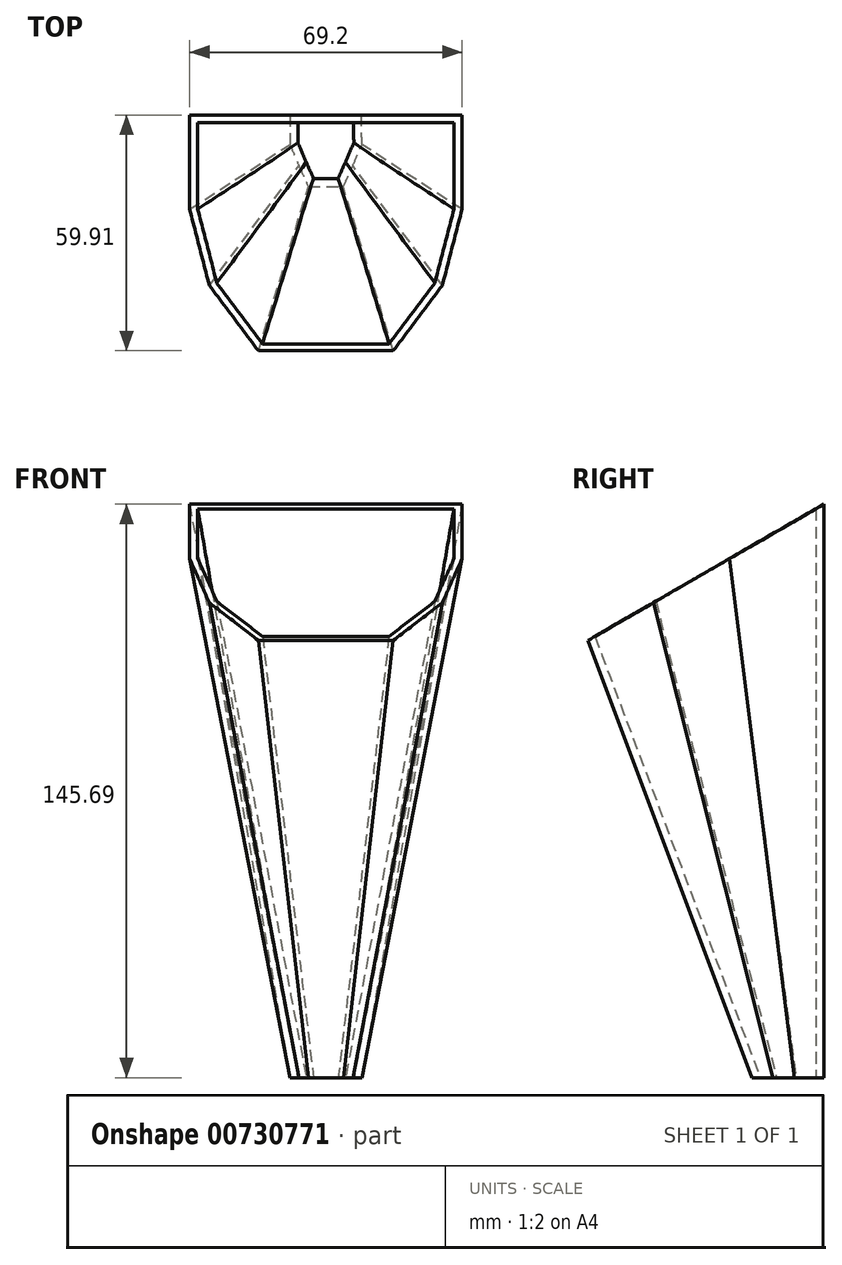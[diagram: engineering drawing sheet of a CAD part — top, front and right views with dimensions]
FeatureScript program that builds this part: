
annotation { "Feature Type Name" : "Feature", "Feature Type Description" : "" }
export const myFeature = defineFeature(function(context is Context, id is Id, definition is map)
    precondition{}
    {
        {
            var Q0;
            Q0=qCreatedBy(makeId("Top.planeOp"),FACE);
            var sketch = newSketch(context, id + "F0", { "sketchPlane" : qUnion([Q0])});
            skLineSegment(sketch, "E0", {"start": v(-50.65, 0) * mm, "end": v(54.5, 0) * mm, "construction": true});
            skSolve(sketch);
        }
        {
            var Q0;
            Q0=sQuery(id+"F0.wireOp",EDGE,"E0");
            cPlane(context, id + "F1", {"entities" : qUnion([Q0]), "cplaneType" : CPlaneType.LINE_ANGLE, "offset" : 25 * mm, "angle" : 300 * degree, "width" : 150 * mm, "height" : 150 * mm});
        }
        {
            var Q0;
            Q0=qCreatedBy(id+"F1.planeOp",FACE);
            var sketch = newSketch(context, id + "F2", { "sketchPlane" : qUnion([Q0])});
            skLineSegment(sketch, "E1", {"start": v(-35, 0) * mm, "end": v(35, 0) * mm});
            skLineSegment(sketch, "E2", {"start": v(35, 0) * mm, "end": v(35, 28) * mm});
            skLineSegment(sketch, "E3", {"start": v(17.35, 70) * mm, "end": v(0, 70) * mm});
            skCircle(sketch, "E4", {"center": v(0, 38) * mm, "radius": 25 * mm, "construction": true});
            skLineSegment(sketch, "E5", {"start": v(17.35, 70) * mm, "end": v(29.98, 50.6) * mm});
            skLineSegment(sketch, "E6", {"start": v(29.98, 50.6) * mm, "end": v(35, 28) * mm});
            skLineSegment(sketch, "E7", {"start": v(0, 0) * mm, "end": v(0, 70) * mm, "construction": true});
            skLineSegment(sketch, "E8.MirrorCS", {"start": v(-35, 0) * mm, "end": v(-35, 28) * mm});
            skLineSegment(sketch, "E9.MirrorCS", {"start": v(-29.98, 50.6) * mm, "end": v(-35, 28) * mm});
            skLineSegment(sketch, "E10.MirrorCS", {"start": v(-17.35, 70) * mm, "end": v(-29.98, 50.6) * mm});
            skLineSegment(sketch, "E11.MirrorCS", {"start": v(-17.35, 70) * mm, "end": v(0, 70) * mm});
            skSolve(sketch);
        }
        {
            var Q0;
            Q0=qCreatedBy(makeId("Top.planeOp"),FACE);
            cPlane(context, id + "F3", {"entities" : qUnion([Q0]), "cplaneType" : CPlaneType.OFFSET, "offset" : 150 * mm, "oppositeDirection" : true, "width" : 150 * mm, "height" : 150 * mm});
        }
        {
            var Q0;
            Q0=qCreatedBy(id+"F3.planeOp",FACE);
            var sketch = newSketch(context, id + "F4", { "sketchPlane" : qUnion([Q0])});
            skLineSegment(sketch, "E12", {"start": v(-8.75, 0) * mm, "end": v(-8.75, -7.25) * mm});
            skLineSegment(sketch, "E13", {"start": v(-4.2, -17.5) * mm, "end": v(0, -17.5) * mm});
            skCircle(sketch, "E14", {"center": v(0, -7.25) * mm, "radius": 6.25 * mm, "construction": true});
            skLineSegment(sketch, "E15", {"start": v(-8.75, 0) * mm, "end": v(0, 0) * mm});
            skLineSegment(sketch, "E16", {"start": v(0, 0) * mm, "end": v(0, -57.56) * mm, "construction": true});
            skLineSegment(sketch, "E17.MirrorCS", {"start": v(8.75, 0) * mm, "end": v(0, 0) * mm});
            skLineSegment(sketch, "E18", {"start": v(-8.75, -7.25) * mm, "end": v(-6.48, -12.38) * mm});
            skLineSegment(sketch, "E19", {"start": v(-6.48, -12.38) * mm, "end": v(-4.2, -17.5) * mm});
            skLineSegment(sketch, "E20.MirrorCS", {"start": v(4.2, -17.5) * mm, "end": v(0, -17.5) * mm});
            skLineSegment(sketch, "E21.MirrorCS", {"start": v(6.48, -12.38) * mm, "end": v(4.2, -17.5) * mm});
            skLineSegment(sketch, "E22.MirrorCS", {"start": v(8.75, -7.25) * mm, "end": v(6.48, -12.38) * mm});
            skLineSegment(sketch, "E23.MirrorCS", {"start": v(8.75, 0) * mm, "end": v(8.75, -7.25) * mm});
            skSolve(sketch);
        }
        {
            var Q0;
            Q0=makeQuery(id+"F2.imprint","IMPRINT",FACE,{"disambiguationData":[TD([[makeQuery(id+"F2.imprint","IMPRINT",EDGE,{"derivedFrom":sQuery(id+"F2.wireOp",EDGE,"E1")}),1.0]])]});
            var Q1;
            Q1=makeQuery(id+"F4.imprint","IMPRINT",FACE,{"disambiguationData":[TD([[makeQuery(id+"F4.imprint","IMPRINT",EDGE,{"derivedFrom":sQuery(id+"F4.wireOp",EDGE,"E12")}),1.0]])]});
            loft(context, id + "F5", {"sheetProfilesArray" : [{ "sheetProfileEntities" : qUnion([Q0]) }, { "sheetProfileEntities" : qUnion([Q1]) }]});
        }
        {
            var Q0;
            Q0=makeQuery(id+"F5.opLoft","SWEPT_FACE",FACE,{"disambiguationData":[OSD([sQuery(id+"F2.wireOp",EDGE,"E2"),sQuery(id+"F2.wireOp",EDGE,"E5"),sQuery(id+"F2.wireOp",EDGE,"E6"),sQuery(id+"F4.wireOp",EDGE,"E21.MirrorCS"),sQuery(id+"F4.wireOp",EDGE,"E22.MirrorCS"),sQuery(id+"F4.wireOp",EDGE,"E23.MirrorCS")])]});
            var Q1;
            Q1=makeQuery(id+"F5.opLoft","SWEPT_FACE",FACE,{"disambiguationData":[OSD([sQuery(id+"F2.wireOp",EDGE,"E1"),sQuery(id+"F2.wireOp",EDGE,"E2"),sQuery(id+"F2.wireOp",EDGE,"E6"),sQuery(id+"F4.wireOp",EDGE,"E17.MirrorCS"),sQuery(id+"F4.wireOp",EDGE,"E22.MirrorCS"),sQuery(id+"F4.wireOp",EDGE,"E23.MirrorCS")])]});
            var Q2;
            Q2=makeQuery(id+"F5.opLoft","SWEPT_FACE",FACE,{"disambiguationData":[OSD([sQuery(id+"F2.wireOp",EDGE,"E3"),sQuery(id+"F2.wireOp",EDGE,"E5"),sQuery(id+"F2.wireOp",EDGE,"E6"),sQuery(id+"F4.wireOp",EDGE,"E20.MirrorCS"),sQuery(id+"F4.wireOp",EDGE,"E21.MirrorCS"),sQuery(id+"F4.wireOp",EDGE,"E22.MirrorCS")])]});
            var Q3;
            Q3=makeQuery(id+"F5.opLoft","SWEPT_BODY",BODY,{"disambiguationData":[OSD([makeQuery(id+"F2.imprint","IMPRINT",FACE,{"disambiguationData":[TD([[makeQuery(id+"F2.imprint","IMPRINT",EDGE,{"derivedFrom":sQuery(id+"F2.wireOp",EDGE,"E1")}),1.0]])]}),makeQuery(id+"F4.imprint","IMPRINT",FACE,{"disambiguationData":[TD([[makeQuery(id+"F4.imprint","IMPRINT",EDGE,{"derivedFrom":sQuery(id+"F4.wireOp",EDGE,"E12")}),1.0]])]})])]});
            shell(context, id + "F6", {"isHollow" : true, "entities" : qUnion([Q0, Q1, Q2]), "parts" : qUnion([Q3]), "thickness" : 2 * mm});
        }
        {
            var Q0;
            Q0=makeQuery(id+"F5.opLoft","CAP_FACE",FACE,{"disambiguationData":[OSD([makeQuery(id+"F2.imprint","IMPRINT",FACE,{"disambiguationData":[TD([[makeQuery(id+"F2.imprint","IMPRINT",EDGE,{"derivedFrom":sQuery(id+"F2.wireOp",EDGE,"E1")}),1.0]])]})])],"isStart":true});
            var sketch = newSketch(context, id + "F7", { "sketchPlane" : qUnion([Q0])});
            skLineSegment(sketch, "E24.0", {"start": v(17.35, -70) * mm, "end": v(-17.35, -70) * mm});
            skLineSegment(sketch, "E24.1", {"start": v(29.98, -50.6) * mm, "end": v(17.35, -70) * mm});
            skLineSegment(sketch, "E24.2", {"start": v(35, -28) * mm, "end": v(29.98, -50.6) * mm});
            skLineSegment(sketch, "E24.3", {"start": v(35, 0) * mm, "end": v(35, -28) * mm});
            skLineSegment(sketch, "E24.4", {"start": v(-29.98, -50.6) * mm, "end": v(-35, -28) * mm});
            skLineSegment(sketch, "E24.5", {"start": v(-17.35, -70) * mm, "end": v(-29.98, -50.6) * mm});
            skLineSegment(sketch, "E24.6", {"start": v(-35, -28) * mm, "end": v(-35, 0) * mm});
            skLineSegment(sketch, "E25", {"start": v(-35, 0) * mm, "end": v(35, 0) * mm});
            skLineSegment(sketch, "E26.0", {"start": v(45, 10) * mm, "end": v(45, -29.1) * mm});
            skLineSegment(sketch, "E26.1", {"start": v(-45, 10) * mm, "end": v(45, 10) * mm});
            skLineSegment(sketch, "E26.2", {"start": v(45, -29.1) * mm, "end": v(39.35, -54.54) * mm});
            skLineSegment(sketch, "E26.3", {"start": v(-45, -29.1) * mm, "end": v(-45, 10) * mm});
            skLineSegment(sketch, "E26.4", {"start": v(39.35, -54.54) * mm, "end": v(22.77, -80) * mm});
            skLineSegment(sketch, "E26.5", {"start": v(22.77, -80) * mm, "end": v(-22.77, -80) * mm});
            skLineSegment(sketch, "E26.6", {"start": v(-22.77, -80) * mm, "end": v(-39.35, -54.54) * mm});
            skLineSegment(sketch, "E26.7", {"start": v(-39.35, -54.54) * mm, "end": v(-45, -29.1) * mm});
            skSolve(sketch);
        }
        {
            var Q0;
            Q0=makeQuery(id+"F7.imprint","IMPRINT",FACE,{"disambiguationData":[TD([[makeQuery(id+"F7.imprint","IMPRINT",EDGE,{"derivedFrom":sQuery(id+"F7.wireOp",EDGE,"E24.0")}),1.0]])]});
            var Q1;
            Q1=makeQuery(id+"F7.imprint","IMPRINT",FACE,{"disambiguationData":[TD([[makeQuery(id+"F7.imprint","IMPRINT",EDGE,{"derivedFrom":sQuery(id+"F7.wireOp",EDGE,"E24.0")}),-1.0]])]});
            extrude(context, id + "F8", {"entities" : qUnion([Q0, Q1]), "operationType" : NewBodyOperationType.REMOVE, "oppositeDirection" : true, "depth" : 2 * mm, "offsetDistance" : 25 * mm});
        }
        {
            var Q0;
            Q0=makeQuery(id+"F5.opLoft","CAP_FACE",FACE,{"disambiguationData":[OSD([makeQuery(id+"F4.imprint","IMPRINT",FACE,{"disambiguationData":[TD([[makeQuery(id+"F4.imprint","IMPRINT",EDGE,{"derivedFrom":sQuery(id+"F4.wireOp",EDGE,"E12")}),1.0]])]})])],"isStart":true});
            var sketch = newSketch(context, id + "F9", { "sketchPlane" : qUnion([Q0])});
            skLineSegment(sketch, "E27.0", {"start": v(-8.75, 7.25) * mm, "end": v(-8.75, 0) * mm});
            skLineSegment(sketch, "E27.1", {"start": v(-6.48, 12.38) * mm, "end": v(-8.75, 7.25) * mm});
            skLineSegment(sketch, "E27.2", {"start": v(-4.2, 17.5) * mm, "end": v(-6.48, 12.38) * mm});
            skLineSegment(sketch, "E27.3", {"start": v(4.2, 17.5) * mm, "end": v(-4.2, 17.5) * mm});
            skLineSegment(sketch, "E27.4", {"start": v(6.48, 12.38) * mm, "end": v(4.2, 17.5) * mm});
            skLineSegment(sketch, "E27.5", {"start": v(8.75, 7.25) * mm, "end": v(6.48, 12.38) * mm});
            skLineSegment(sketch, "E27.6", {"start": v(8.75, 0) * mm, "end": v(8.75, 7.25) * mm});
            skPoint(sketch, "E27.7", {"position": v(8.75, 3.62) * mm});
            skLineSegment(sketch, "E28", {"start": v(-8.75, 0) * mm, "end": v(8.75, 0) * mm});
            skLineSegment(sketch, "E29.0", {"start": v(18.75, -10) * mm, "end": v(18.75, 9.37) * mm});
            skLineSegment(sketch, "E29.1", {"start": v(-18.75, -10) * mm, "end": v(18.75, -10) * mm});
            skLineSegment(sketch, "E29.2", {"start": v(18.75, 9.37) * mm, "end": v(15.62, 16.43) * mm});
            skLineSegment(sketch, "E29.3", {"start": v(-18.75, 9.37) * mm, "end": v(-18.75, -10) * mm});
            skLineSegment(sketch, "E29.4", {"start": v(15.62, 16.43) * mm, "end": v(10.72, 27.5) * mm});
            skLineSegment(sketch, "E29.5", {"start": v(10.72, 27.5) * mm, "end": v(-10.72, 27.5) * mm});
            skLineSegment(sketch, "E29.6", {"start": v(-10.72, 27.5) * mm, "end": v(-15.62, 16.43) * mm});
            skLineSegment(sketch, "E29.7", {"start": v(-15.62, 16.43) * mm, "end": v(-18.75, 9.37) * mm});
            skFitSpline(sketch, "E30.0", {"points": [v(6.03, 11.45) * mm, v(14.64, 17.02) * mm, v(23.26, 22.6) * mm, v(31.87, 28.18) * mm]});
            skFitSpline(sketch, "E30.1", {"points": [v(33.6, 40.32) * mm, v(25.9, 30) * mm, v(18.2, 19.7) * mm, v(10.48, 9.38) * mm]});
            skFitSpline(sketch, "E30.2", {"points": [v(29.74, 22.73) * mm, v(28.08, 29.18) * mm, v(26.42, 35.62) * mm, v(24.76, 42.06) * mm]});
            skSolve(sketch);
        }
        {
            var Q0;
            Q0=makeQuery(id+"F9.imprint","IMPRINT",FACE,{"disambiguationData":[TD([[makeQuery(id+"F9.imprint","IMPRINT",EDGE,{"derivedFrom":sQuery(id+"F9.wireOp",EDGE,"E27.0")}),-1.0]])]});
            var Q1;
            Q1=makeQuery(id+"F9.imprint","IMPRINT",FACE,{"disambiguationData":[TD([[makeQuery(id+"F9.imprint","IMPRINT",EDGE,{"derivedFrom":sQuery(id+"F9.wireOp",EDGE,"E27.0")}),1.0]])]});
            extrude(context, id + "F10", {"entities" : qUnion([Q0, Q1]), "operationType" : NewBodyOperationType.REMOVE, "oppositeDirection" : true, "depth" : 2 * mm, "offsetDistance" : 25 * mm});
        }
    });
